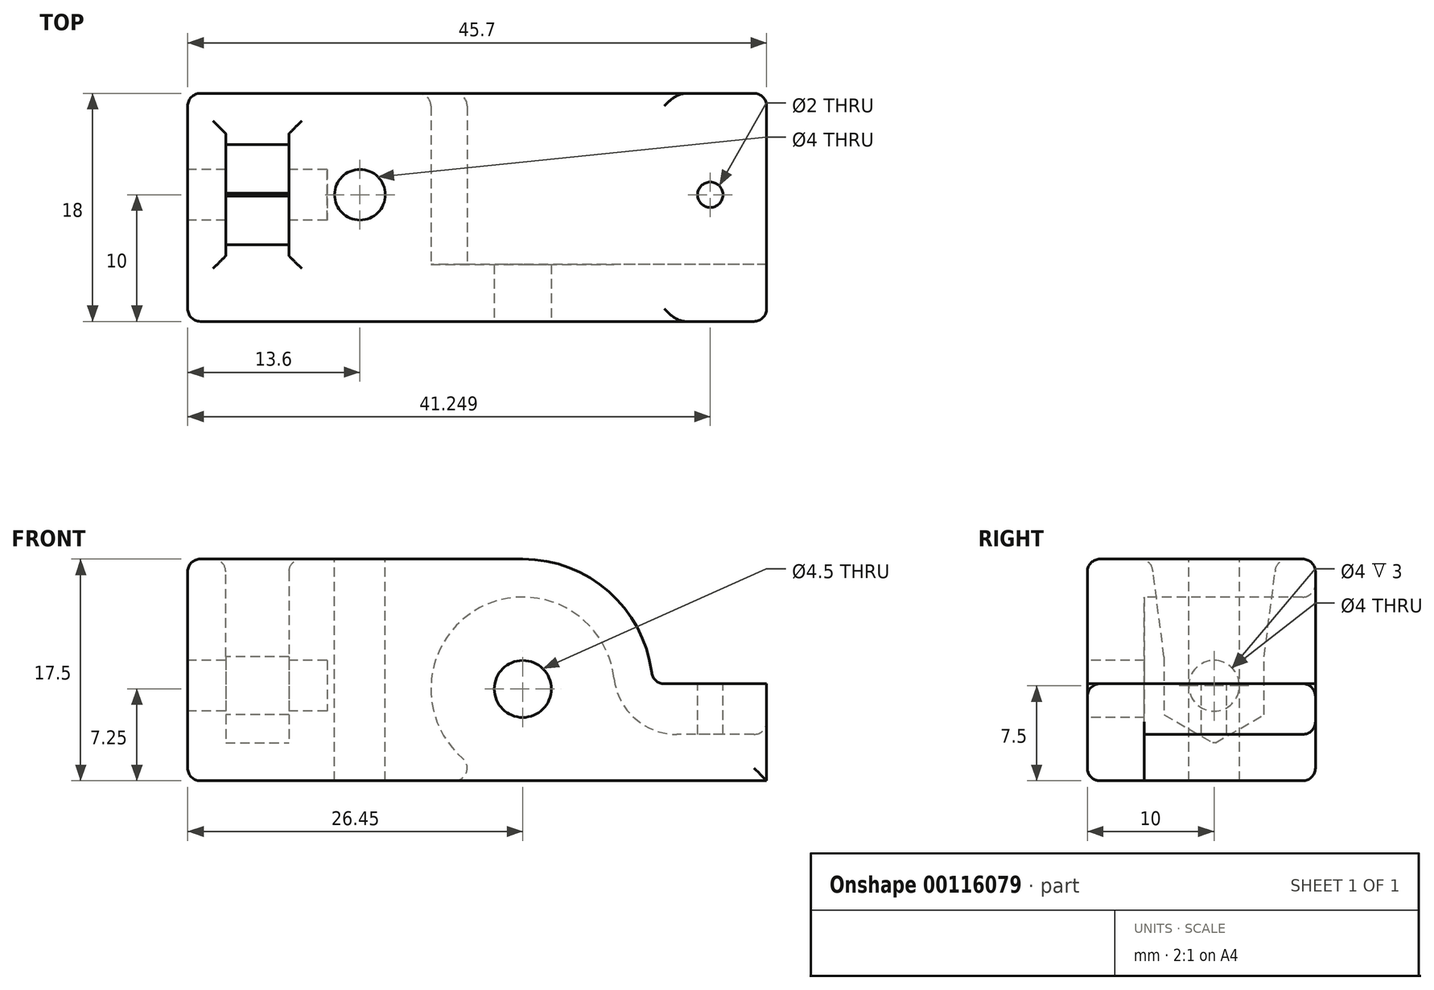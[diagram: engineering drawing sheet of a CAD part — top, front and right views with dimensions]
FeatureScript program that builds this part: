
annotation { "Feature Type Name" : "Feature", "Feature Type Description" : "" }
export const myFeature = defineFeature(function(context is Context, id is Id, definition is map)
    precondition{}
    {
        {
            var Q0;
            Q0=qCreatedBy(makeId("Front.planeOp"),FACE);
            var sketch = newSketch(context, id + "F0", { "sketchPlane" : qUnion([Q0])});
            skLineSegment(sketch, "E0.bottom", {"start": v(-4.4, 17.5) * mm, "end": v(4.4, 17.5) * mm, "construction": true});
            skLineSegment(sketch, "E0.top", {"start": v(-4.4, 21) * mm, "end": v(4.4, 21) * mm, "construction": true});
            skLineSegment(sketch, "E0.left", {"start": v(-4.4, 17.5) * mm, "end": v(-4.4, 21) * mm, "construction": true});
            skLineSegment(sketch, "E0.right", {"start": v(4.4, 17.5) * mm, "end": v(4.4, 21) * mm, "construction": true});
            skLineSegment(sketch, "E1", {"start": v(0, 17.5) * mm, "end": v(0, 0) * mm, "construction": true});
            skLineSegment(sketch, "E2", {"start": v(2.6, 17.5) * mm, "end": v(2.6, 0) * mm, "construction": true});
            skLineSegment(sketch, "E3.MirrorCS", {"start": v(-2.6, 17.5) * mm, "end": v(-2.6, 0) * mm, "construction": true});
            skLineSegment(sketch, "E4.bottom", {"start": v(32.1, 0) * mm, "end": v(-13.6, 0) * mm});
            skLineSegment(sketch, "E4.top", {"start": v(32.1, 17.5) * mm, "end": v(-13.6, 17.5) * mm});
            skLineSegment(sketch, "E4.left", {"start": v(32.1, 0) * mm, "end": v(32.1, 17.5) * mm});
            skLineSegment(sketch, "E4.right", {"start": v(-13.6, 0) * mm, "end": v(-13.6, 17.5) * mm});
            skLineSegment(sketch, "E5", {"start": v(-10.6, 17.5) * mm, "end": v(-10.6, 0) * mm});
            skLineSegment(sketch, "E6", {"start": v(-5.6, 17.5) * mm, "end": v(-5.6, 0) * mm});
            skLineSegment(sketch, "E7", {"start": v(-10.6, 3) * mm, "end": v(-5.6, 3) * mm});
            skLineSegment(sketch, "E8.MirrorCS", {"start": v(-10.6, 12) * mm, "end": v(-5.6, 12) * mm, "construction": true});
            skCircle(sketch, "E9", {"center": v(12.85, 7.25) * mm, "radius": 4.5 * mm});
            skLineSegment(sketch, "E10", {"start": v(32.1, 1.26) * mm, "end": v(36.53, 1.26) * mm, "construction": true});
            skLineSegment(sketch, "E11", {"start": v(32.1, 2.4) * mm, "end": v(36.74, 2.4) * mm, "construction": true});
            skLineSegment(sketch, "E12", {"start": v(32.1, 3.66) * mm, "end": v(36.94, 3.66) * mm, "construction": true});
            skLineSegment(sketch, "E13", {"start": v(32.1, 0) * mm, "end": v(35.76, 0) * mm, "construction": true});
            skCircle(sketch, "E14", {"center": v(12.85, 7.25) * mm, "radius": 7.25 * mm});
            skLineSegment(sketch, "E15", {"start": v(12.85, 0) * mm, "end": v(32.1, 0) * mm});
            skLineSegment(sketch, "E16", {"start": v(32.1, 3.66) * mm, "end": v(19.15, 3.66) * mm});
            skLineSegment(sketch, "E17", {"start": v(-5.6, 10.1) * mm, "end": v(-13.6, 10.1) * mm});
            skLineSegment(sketch, "E18.MirrorCS", {"start": v(-5.6, 4.9) * mm, "end": v(-13.6, 4.9) * mm});
            skPoint(sketch, "E19.orphan", {"position": v(-5.6, 10.1) * mm});
            skPoint(sketch, "E20.orphan", {"position": v(-10.6, 10.1) * mm});
            skLineSegment(sketch, "E21", {"start": v(-13.6, 7.5) * mm, "end": v(-24.03, 7.5) * mm, "construction": true});
            skArc(sketch, "E22.0", {"start": v(23.1, 7.66) * mm, "mid": v(19.95, 14.64) * mm, "end": v(12.85, 17.5) * mm});
            skLineSegment(sketch, "E23", {"start": v(32.1, 7.66) * mm, "end": v(23.1, 7.66) * mm});
            skSolve(sketch);
        }
        {
            var Q0;
            {var subQ1=sQuery(id+"F0.wireOp",EDGE,"E4.bottom");var subQ6=sQuery(id+"F0.wireOp",EDGE,"E4.right");var subQ7=makeQuery(id+"F0.imprint","INTERSECT",VERTEX,{"derivedFrom":[subQ1,subQ6]});Q0=makeQuery(id+"F0.imprint","IMPRINT",FACE,{"disambiguationData":[TD([[makeQuery(id+"F0.imprint","IMPRINT",EDGE,{"disambiguationData":[TD([[subQ7,1.0]])],"derivedFrom":subQ1}),-1.0]])]});}
            var Q1;
            {var subQ5=sQuery(id+"F0.wireOp",EDGE,"E7");Q1=makeQuery(id+"F0.imprint","IMPRINT",FACE,{"disambiguationData":[TD([[makeQuery(id+"F0.imprint","IMPRINT",EDGE,{"derivedFrom":subQ5}),-1.0]])]});}
            var Q2;
            {var subQ3=sQuery(id+"F0.wireOp",EDGE,"E16");Q2=makeQuery(id+"F0.imprint","IMPRINT",FACE,{"disambiguationData":[TD([[makeQuery(id+"F0.imprint","IMPRINT",EDGE,{"derivedFrom":subQ3}),-1.0]])]});}
            var Q3;
            {var subQ0=sQuery(id+"F0.wireOp",EDGE,"E17");var subQ1=sQuery(id+"F0.wireOp",EDGE,"E4.right");var subQ2=makeQuery(id+"F0.imprint","INTERSECT",VERTEX,{"derivedFrom":[subQ1,subQ0]});Q3=makeQuery(id+"F0.imprint","IMPRINT",FACE,{"disambiguationData":[TD([[makeQuery(id+"F0.imprint","IMPRINT",EDGE,{"disambiguationData":[TD([[subQ2,1.0]])],"derivedFrom":subQ1}),-1.0]])]});}
            var Q4;
            {var subQ0=sQuery(id+"F0.wireOp",EDGE,"E4.right");var subQ1=sQuery(id+"F0.wireOp",EDGE,"E4.top");var subQ2=makeQuery(id+"F0.imprint","INTERSECT",VERTEX,{"derivedFrom":[subQ1,subQ0]});Q4=makeQuery(id+"F0.imprint","IMPRINT",FACE,{"disambiguationData":[TD([[makeQuery(id+"F0.imprint","IMPRINT",EDGE,{"disambiguationData":[TD([[subQ2,1.0]])],"derivedFrom":subQ1}),1.0]])]});}
            var Q5;
            {var subQ3=sQuery(id+"F0.wireOp",EDGE,"E22.0");Q5=makeQuery(id+"F0.imprint","IMPRINT",FACE,{"disambiguationData":[TD([[makeQuery(id+"F0.imprint","IMPRINT",EDGE,{"derivedFrom":subQ3}),-1.0]])]});}
            extrude(context, id + "F1", {"entities" : qUnion([Q0, Q1, Q2, Q3, Q4, Q5]), "oppositeDirection" : true, "depth" : 8 * mm, "offsetDistance" : 25 * mm, "hasSecondDirection" : true, "secondDirectionOppositeDirection" : false, "secondDirectionDepth" : 10 * mm});
        }
        {
            var Q0;
            Q0=makeQuery(id+"F1.opExtrude","SWEPT_FACE",FACE,{"disambiguationData":[OSD([sQuery(id+"F0.wireOp",EDGE,"E4.right")])]});
            var sketch = newSketch(context, id + "F2", { "sketchPlane" : qUnion([Q0])});
            skLineSegment(sketch, "E24", {"start": v(0, 0) * mm, "end": v(0, 17.5) * mm, "construction": true});
            skCircle(sketch, "E25", {"center": v(0, 7.5) * mm, "radius": 2.6 * mm, "construction": true});
            skPoint(sketch, "E26.0", {"position": v(0, 12) * mm});
            skPoint(sketch, "E27.0", {"position": v(0, 3) * mm});
            skCircle(sketch, "E28.cCircle", {"center": v(0, 7.5) * mm, "radius": 3.95 * mm, "construction": true});
            skLineSegment(sketch, "E28.0", {"start": v(3.95, 9.78) * mm, "end": v(3.95, 0) * mm});
            skLineSegment(sketch, "E28.1", {"start": v(3.95, 5.22) * mm, "end": v(0, 2.94) * mm});
            skLineSegment(sketch, "E28.2", {"start": v(0, 2.94) * mm, "end": v(-3.95, 5.22) * mm});
            skLineSegment(sketch, "E28.3", {"start": v(-3.95, 0) * mm, "end": v(-3.95, 9.78) * mm});
            skLineSegment(sketch, "E28.4", {"start": v(-3.95, 9.78) * mm, "end": v(0, 12.06) * mm});
            skLineSegment(sketch, "E28.5", {"start": v(0, 12.06) * mm, "end": v(3.95, 9.78) * mm});
            skPoint(sketch, "E28.0.midPoint", {"position": v(3.95, 7.5) * mm});
            skLineSegment(sketch, "E29.bottom", {"start": v(10, 17.5) * mm, "end": v(5.5, 17.5) * mm});
            skLineSegment(sketch, "E29.top", {"start": v(10, 0) * mm, "end": v(5.5, 0) * mm});
            skLineSegment(sketch, "E29.left", {"start": v(10, 17.5) * mm, "end": v(10, 0) * mm});
            skLineSegment(sketch, "E29.right", {"start": v(5.5, 17.5) * mm, "end": v(5.5, 0) * mm});
            skLineSegment(sketch, "E30.0", {"start": v(-8, 0) * mm, "end": v(-8, 17.5) * mm});
            skLineSegment(sketch, "E31", {"start": v(3.95, 9.78) * mm, "end": v(4.95, 17.5) * mm});
            skLineSegment(sketch, "E32", {"start": v(4.95, 17.5) * mm, "end": v(5.5, 17.5) * mm});
            skLineSegment(sketch, "E33.MirrorCS", {"start": v(-3.95, 9.78) * mm, "end": v(-4.95, 17.5) * mm});
            skLineSegment(sketch, "E34.MirrorCS", {"start": v(-4.95, 17.5) * mm, "end": v(-5.5, 17.5) * mm});
            skLineSegment(sketch, "E35.0", {"start": v(-8, 0) * mm, "end": v(10, 0) * mm});
            skLineSegment(sketch, "E36.bottom", {"start": v(-4.5, 2.4) * mm, "end": v(4.5, 2.4) * mm});
            skLineSegment(sketch, "E36.top", {"start": v(-4.5, 0) * mm, "end": v(4.5, 0) * mm});
            skLineSegment(sketch, "E36.left", {"start": v(-4.5, 2.4) * mm, "end": v(-4.5, 0) * mm});
            skLineSegment(sketch, "E36.right", {"start": v(4.5, 2.4) * mm, "end": v(4.5, 0) * mm});
            skPoint(sketch, "E36.middle", {"position": v(0, 1.2) * mm});
            skCircle(sketch, "E37", {"center": v(0, 7.5) * mm, "radius": 2 * mm});
            skLineSegment(sketch, "E38.bottom", {"start": v(12, 11.2) * mm, "end": v(8.5, 11.2) * mm});
            skLineSegment(sketch, "E38.top", {"start": v(12, 3.3) * mm, "end": v(8.5, 3.3) * mm});
            skLineSegment(sketch, "E38.left", {"start": v(12, 11.2) * mm, "end": v(12, 3.3) * mm});
            skLineSegment(sketch, "E38.right", {"start": v(8.5, 11.2) * mm, "end": v(8.5, 3.3) * mm});
            skPoint(sketch, "E39.0", {"position": v(0, 7.25) * mm});
            skLineSegment(sketch, "E40", {"start": v(0, 7.25) * mm, "end": v(15.95, 7.25) * mm, "construction": true});
            skSolve(sketch);
        }
        {
            var Q0;
            Q0=makeQuery(id+"F2.imprint","IMPRINT",FACE,{"disambiguationData":[TD([[makeQuery(id+"F2.imprint","IMPRINT",EDGE,{"derivedFrom":sQuery(id+"F2.wireOp",EDGE,"E37")}),1.0]])]});
            var Q1;
            Q1=sQuery(id+"F6.wireOp",EDGE,"IWxHj1E6-c78I-Bpa6-nnZ4-fiathDjzlDGy");
            var Q2;
            Q2=sQuery(id+"F6.wireOp",EDGE,"G7mef5TC-vuGq-qOCV-Zkp3-S8K1r66uwu5S");
            var Q3;
            Q3=makeQuery(id+"F1.opExtrude","SWEPT_FACE",FACE,{"disambiguationData":[OSD([sQuery(id+"F0.wireOp",EDGE,"E6")])]});
            extrude(context, id + "F3", {"entities" : qUnion([Q0]), "operationType" : NewBodyOperationType.REMOVE, "surfaceEntities" : qUnion([Q1, Q2]), "endBound" : BoundingType.UP_TO_SURFACE, "oppositeDirection" : true, "depth" : 25 * mm, "endBoundEntityFace" : qUnion([Q3]), "hasOffset" : true, "offsetDistance" : 3 * mm, "offsetOppositeDirection" : true});
        }
        {
            var Q0;
            {var subQ0=sQuery(id+"F2.wireOp",EDGE,"E30.0");Q0=makeQuery(id+"F2.imprint","IMPRINT",FACE,{"disambiguationData":[TD([[makeQuery(id+"F2.imprint","IMPRINT",EDGE,{"derivedFrom":subQ0}),-1.0]])]});}
            var Q1;
            {var subQ5=sQuery(id+"F2.wireOp",EDGE,"E29.right");Q1=makeQuery(id+"F2.imprint","IMPRINT",FACE,{"disambiguationData":[TD([[makeQuery(id+"F2.imprint","IMPRINT",EDGE,{"derivedFrom":subQ5}),-1.0]])]});}
            var Q2;
            {var subQ4=sQuery(id+"F2.wireOp",EDGE,"E28.1");Q2=makeQuery(id+"F2.imprint","IMPRINT",FACE,{"disambiguationData":[TD([[makeQuery(id+"F2.imprint","IMPRINT",EDGE,{"derivedFrom":subQ4}),1.0]])]});}
            var Q3;
            Q3=makeQuery(id+"F1.opExtrude","SWEPT_FACE",FACE,{"disambiguationData":[OSD([sQuery(id+"F0.wireOp",EDGE,"E6")])]});
            extrude(context, id + "F4", {"entities" : qUnion([Q0, Q1, Q2]), "operationType" : NewBodyOperationType.ADD, "endBound" : BoundingType.UP_TO_SURFACE, "oppositeDirection" : true, "depth" : 25 * mm, "endBoundEntityFace" : qUnion([Q3]), "offsetDistance" : 25 * mm});
        }
        {
            var Q0;
            {var subQ2=sQuery(id+"F2.wireOp",EDGE,"E29.bottom");Q0=makeQuery(id+"F2.imprint","IMPRINT",FACE,{"disambiguationData":[TD([[makeQuery(id+"F2.imprint","IMPRINT",EDGE,{"derivedFrom":subQ2}),-1.0]])]});}
            var Q1;
            {var subQ5=sQuery(id+"F2.wireOp",EDGE,"E38.right");Q1=makeQuery(id+"F2.imprint","IMPRINT",FACE,{"disambiguationData":[TD([[makeQuery(id+"F2.imprint","IMPRINT",EDGE,{"derivedFrom":subQ5}),1.0]])]});}
            var Q2;
            {var subQ0=sQuery(id+"F0.wireOp",EDGE,"E4.left");Q2=makeQuery(id+"F1.opExtrude","SWEPT_FACE",FACE,{"disambiguationData":[OSD([subQ0]),TDD([makeQuery(id+"F0.imprint","IMPRINT",EDGE,{"disambiguationData":[TD([[makeQuery(id+"F0.imprint","INTERSECT",VERTEX,{"derivedFrom":[subQ0,sQuery(id+"F0.wireOp",EDGE,"E16")]}),-1.0]])],"derivedFrom":subQ0})])]});}
            extrude(context, id + "F5", {"entities" : qUnion([Q0, Q1]), "operationType" : NewBodyOperationType.ADD, "endBound" : BoundingType.UP_TO_SURFACE, "oppositeDirection" : true, "depth" : 7 * mm, "endBoundEntityFace" : qUnion([Q2]), "offsetDistance" : 2 * mm});
        }
        {
            var Q0;
            {var subQ0=sQuery(id+"F0.wireOp",EDGE,"E4.left");Q0=makeQuery(id+"F5.boolean.opBoolean","MERGE",FACE,{"derivedFrom":[makeQuery(id+"F1.opExtrude","SWEPT_FACE",FACE,{"disambiguationData":[OSD([subQ0]),TDD([makeQuery(id+"F0.imprint","IMPRINT",EDGE,{"disambiguationData":[TD([[makeQuery(id+"F0.imprint","INTERSECT",VERTEX,{"derivedFrom":[sQuery(id+"F0.wireOp",EDGE,"E4.bottom"),subQ0]}),-1.0]])],"derivedFrom":subQ0})])]}),makeQuery(id+"F1.opExtrude","SWEPT_FACE",FACE,{"disambiguationData":[OSD([subQ0]),TDD([makeQuery(id+"F0.imprint","IMPRINT",EDGE,{"disambiguationData":[TD([[makeQuery(id+"F0.imprint","INTERSECT",VERTEX,{"derivedFrom":[sQuery(id+"F0.wireOp",EDGE,"E4.top"),subQ0]}),1.0]])],"derivedFrom":subQ0})])]}),makeQuery(id+"F5.opExtrude","CAP_FACE",FACE,{"disambiguationData":[OSD([sQuery(id+"F2.wireOp",EDGE,"E29.bottom"),sQuery(id+"F2.wireOp",EDGE,"E29.left"),sQuery(id+"F2.wireOp",EDGE,"E29.right"),sQuery(id+"F2.wireOp",EDGE,"E35.0")])],"isStart":false})]});}
            var sketch = newSketch(context, id + "F6", { "sketchPlane" : qUnion([Q0])});
            skLineSegment(sketch, "E41", {"start": v(0, 0) * mm, "end": v(0, 10.25) * mm, "construction": true});
            skLineSegment(sketch, "E42.bottom", {"start": v(4.5, 17.5) * mm, "end": v(-4.5, 17.5) * mm, "construction": true});
            skLineSegment(sketch, "E42.top", {"start": v(4.5, 18.76) * mm, "end": v(-4.5, 18.76) * mm, "construction": true});
            skLineSegment(sketch, "E42.left", {"start": v(4.5, 17.5) * mm, "end": v(4.5, 18.76) * mm, "construction": true});
            skLineSegment(sketch, "E42.right", {"start": v(-4.5, 17.5) * mm, "end": v(-4.5, 18.76) * mm, "construction": true});
            skPoint(sketch, "E42.middle", {"position": v(0, 18.13) * mm});
            skLineSegment(sketch, "E43", {"start": v(-4.5, 18.76) * mm, "end": v(-4.5, 19.9) * mm, "construction": true});
            skLineSegment(sketch, "E44", {"start": v(-4.5, 19.9) * mm, "end": v(4.5, 19.9) * mm, "construction": true});
            skLineSegment(sketch, "E45", {"start": v(4.5, 19.9) * mm, "end": v(4.5, 18.76) * mm, "construction": true});
            skLineSegment(sketch, "E46", {"start": v(-4.5, 19.9) * mm, "end": v(-4.5, 21.16) * mm, "construction": true});
            skLineSegment(sketch, "E47", {"start": v(-4.5, 21.16) * mm, "end": v(4.5, 21.16) * mm, "construction": true});
            skLineSegment(sketch, "E48", {"start": v(4.5, 21.16) * mm, "end": v(4.5, 19.9) * mm, "construction": true});
            skCircle(sketch, "E49.0", {"center": v(0, 7.5) * mm, "radius": 2 * mm, "construction": true});
            skSolve(sketch);
        }
        {
            var Q0;
            {var subQ0=sQuery(id+"F0.wireOp",EDGE,"E4.right");var subQ1=sQuery(id+"F0.wireOp",EDGE,"E4.top");Q0=makeQuery(id+"F5.boolean.opBoolean","MERGE",FACE,{"derivedFrom":[makeQuery(id+"F4.boolean.opBoolean","MERGE",FACE,{"derivedFrom":[makeQuery(id+"F1.opExtrude","SWEPT_FACE",FACE,{"disambiguationData":[OSD([subQ1]),TDD([makeQuery(id+"F0.imprint","IMPRINT",EDGE,{"disambiguationData":[TD([[makeQuery(id+"F0.imprint","INTERSECT",VERTEX,{"derivedFrom":[subQ1,sQuery(id+"F0.wireOp",EDGE,"E4.left")]}),-1.0]])],"derivedFrom":subQ1})])]}),makeQuery(id+"F1.opExtrude","SWEPT_FACE",FACE,{"disambiguationData":[OSD([subQ1]),TDD([makeQuery(id+"F0.imprint","IMPRINT",EDGE,{"disambiguationData":[TD([[makeQuery(id+"F0.imprint","INTERSECT",VERTEX,{"derivedFrom":[subQ1,subQ0]}),1.0]])],"derivedFrom":subQ1})])]}),makeQuery(id+"F4.opExtrude","SWEPT_FACE",FACE,{"disambiguationData":[OSD([sQuery(id+"F2.wireOp",EDGE,"E32")])]}),makeQuery(id+"F4.opExtrude","SWEPT_FACE",FACE,{"disambiguationData":[OSD([subQ1,subQ0,sQuery(id+"F2.wireOp",EDGE,"E34.MirrorCS")])]})]}),makeQuery(id+"F5.opExtrude","SWEPT_FACE",FACE,{"disambiguationData":[OSD([sQuery(id+"F2.wireOp",EDGE,"E29.bottom")])]})]});}
            var sketch = newSketch(context, id + "F7", { "sketchPlane" : qUnion([Q0])});
            skCircle(sketch, "E50", {"center": v(0, 0) * mm, "radius": 2 * mm});
            skLineSegment(sketch, "E51.0", {"start": v(19.15, 8) * mm, "end": v(19.15, -5.5) * mm, "construction": true});
            skLineSegment(sketch, "E52", {"start": v(19.15, 0) * mm, "end": v(36.15, 0) * mm, "construction": true});
            skCircle(sketch, "E53", {"center": v(27.65, 0) * mm, "radius": 1 * mm});
            skCircle(sketch, "E54", {"center": v(27.65, 0) * mm, "radius": 3 * mm, "construction": true});
            skSolve(sketch);
        }
        {
            var Q0;
            Q0=makeQuery(id+"F7.imprint","IMPRINT",FACE,{"disambiguationData":[TD([[makeQuery(id+"F7.imprint","IMPRINT",EDGE,{"derivedFrom":sQuery(id+"F7.wireOp",EDGE,"E50")}),1.0]])]});
            var Q1;
            Q1=makeQuery(id+"F7.imprint","IMPRINT",FACE,{"disambiguationData":[TD([[makeQuery(id+"F7.imprint","IMPRINT",EDGE,{"derivedFrom":sQuery(id+"F7.wireOp",EDGE,"E53")}),1.0]])]});
            extrude(context, id + "F8", {"entities" : qUnion([Q0, Q1]), "operationType" : NewBodyOperationType.REMOVE, "oppositeDirection" : true, "depth" : 25 * mm, "offsetDistance" : 25 * mm});
        }
        {
            var Q0;
            {var subQ3=sQuery(id+"F0.wireOp",EDGE,"E22.0");Q0=makeQuery(id+"F0.imprint","IMPRINT",FACE,{"disambiguationData":[TD([[makeQuery(id+"F0.imprint","IMPRINT",EDGE,{"derivedFrom":subQ3}),-1.0]])]});}
            extrude(context, id + "F9", {"entities" : qUnion([Q0]), "operationType" : NewBodyOperationType.REMOVE, "endBound" : BoundingType.SYMMETRIC, "depth" : 25 * mm, "offsetDistance" : 25 * mm});
        }
        {
            var Q0;
            Q0=makeQuery(id+"F5.boolean.opBoolean","MERGE",FACE,{"derivedFrom":[makeQuery(id+"F1.opExtrude","CAP_FACE",FACE,{"disambiguationData":[OSD([sQuery(id+"F0.wireOp",EDGE,"E4.bottom"),sQuery(id+"F0.wireOp",EDGE,"E4.top"),sQuery(id+"F0.wireOp",EDGE,"E4.left"),sQuery(id+"F0.wireOp",EDGE,"E4.right"),sQuery(id+"F0.wireOp",EDGE,"E5"),sQuery(id+"F0.wireOp",EDGE,"E6"),sQuery(id+"F0.wireOp",EDGE,"E7"),sQuery(id+"F0.wireOp",EDGE,"E14"),sQuery(id+"F0.wireOp",EDGE,"E15"),sQuery(id+"F0.wireOp",EDGE,"E16")])],"isStart":true}),makeQuery(id+"F5.opExtrude","SWEPT_FACE",FACE,{"disambiguationData":[OSD([sQuery(id+"F2.wireOp",EDGE,"E29.left")])]})]});
            var sketch = newSketch(context, id + "F10", { "sketchPlane" : qUnion([Q0])});
            skCircle(sketch, "E55.0", {"center": v(12.85, 7.25) * mm, "radius": 4.5 * mm, "construction": true});
            skCircle(sketch, "E56", {"center": v(12.85, 7.25) * mm, "radius": 2.25 * mm});
            skCircle(sketch, "E57.cCircle", {"center": v(12.85, 7.25) * mm, "radius": 4.25 * mm, "construction": true});
            skLineSegment(sketch, "E57.0", {"start": v(17.1, 9.7) * mm, "end": v(17.1, 4.8) * mm});
            skLineSegment(sketch, "E57.1", {"start": v(17.1, 4.8) * mm, "end": v(12.85, 2.34) * mm});
            skLineSegment(sketch, "E57.2", {"start": v(12.85, 2.34) * mm, "end": v(8.6, 4.8) * mm});
            skLineSegment(sketch, "E57.3", {"start": v(8.6, 4.8) * mm, "end": v(8.6, 9.7) * mm});
            skLineSegment(sketch, "E57.4", {"start": v(8.6, 9.7) * mm, "end": v(12.85, 12.16) * mm});
            skLineSegment(sketch, "E57.5", {"start": v(12.85, 12.16) * mm, "end": v(17.1, 9.7) * mm});
            skPoint(sketch, "E57.0.midPoint", {"position": v(17.1, 7.25) * mm});
            skSolve(sketch);
        }
        {
            var Q0;
            Q0=makeQuery(id+"F10.imprint","IMPRINT",FACE,{"disambiguationData":[TD([[makeQuery(id+"F10.imprint","IMPRINT",EDGE,{"derivedFrom":sQuery(id+"F10.wireOp",EDGE,"E56")}),1.0]])]});
            extrude(context, id + "F11", {"entities" : qUnion([Q0]), "operationType" : NewBodyOperationType.REMOVE, "oppositeDirection" : true, "depth" : 25 * mm, "offsetDistance" : 25 * mm});
        }
        {
            var Q0;
            Q0=makeQuery(id+"F1.opExtrude","SWEPT_EDGE",EDGE,{"disambiguationData":[OSD([sQuery(id+"F0.wireOp",EDGE,"E14"),sQuery(id+"F0.wireOp",EDGE,"E16")])]});
            fillet(context, id + "F12", {"entities" : qUnion([Q0]), "radius" : 5 * mm, "tangentPropagation" : true, "allowEdgeOverflow" : false});
        }
        {
            var Q0;
            Q0=makeQuery(id+"F1.opExtrude","CAP_EDGE",EDGE,{"disambiguationData":[OSD([sQuery(id+"F0.wireOp",EDGE,"E14")])],"isStart":false});
            var Q1;
            {var subQ0=sQuery(id+"F0.wireOp",EDGE,"E16");var subQ1=sQuery(id+"F0.wireOp",EDGE,"E14");Q1=makeQuery(id+"F12.opFillet","BLEND_EDGE",EDGE,{"blendedFrom":[makeQuery(id+"F1.opExtrude","SWEPT_EDGE",EDGE,{"disambiguationData":[OSD([subQ1,subQ0])]}),makeQuery(id+"F4.boolean.opBoolean","MERGE",FACE,{"derivedFrom":[makeQuery(id+"F1.opExtrude","CAP_FACE",FACE,{"disambiguationData":[OSD([sQuery(id+"F0.wireOp",EDGE,"E4.bottom"),sQuery(id+"F0.wireOp",EDGE,"E4.top"),sQuery(id+"F0.wireOp",EDGE,"E4.left"),sQuery(id+"F0.wireOp",EDGE,"E4.right"),sQuery(id+"F0.wireOp",EDGE,"E5"),sQuery(id+"F0.wireOp",EDGE,"E6"),sQuery(id+"F0.wireOp",EDGE,"E7"),subQ1,subQ0,sQuery(id+"F0.wireOp",EDGE,"E22.0"),sQuery(id+"F0.wireOp",EDGE,"E23")])],"isStart":false}),makeQuery(id+"F4.opExtrude","SWEPT_FACE",FACE,{"disambiguationData":[OSD([sQuery(id+"F2.wireOp",EDGE,"E30.0")])]})]})],"blendedInto":[makeQuery(id+"F4.boolean.opBoolean","MERGE",FACE,{"derivedFrom":[makeQuery(id+"F1.opExtrude","CAP_FACE",FACE,{"disambiguationData":[OSD([sQuery(id+"F0.wireOp",EDGE,"E4.bottom"),sQuery(id+"F0.wireOp",EDGE,"E4.top"),sQuery(id+"F0.wireOp",EDGE,"E4.left"),sQuery(id+"F0.wireOp",EDGE,"E4.right"),sQuery(id+"F0.wireOp",EDGE,"E5"),sQuery(id+"F0.wireOp",EDGE,"E6"),sQuery(id+"F0.wireOp",EDGE,"E7"),subQ1,subQ0,sQuery(id+"F0.wireOp",EDGE,"E22.0"),sQuery(id+"F0.wireOp",EDGE,"E23")])],"isStart":false}),makeQuery(id+"F4.opExtrude","SWEPT_FACE",FACE,{"disambiguationData":[OSD([sQuery(id+"F2.wireOp",EDGE,"E30.0")])]})]})]});}
            var Q2;
            {var subQ0=sQuery(id+"F0.wireOp",EDGE,"E4.right");var subQ1=sQuery(id+"F0.wireOp",EDGE,"E4.top");Q2=makeQuery(id+"F4.boolean.opBoolean","MERGE",EDGE,{"derivedFrom":[makeQuery(id+"F1.opExtrude","CAP_EDGE",EDGE,{"disambiguationData":[OSD([subQ1]),TDD([makeQuery(id+"F0.imprint","IMPRINT",EDGE,{"disambiguationData":[TD([[makeQuery(id+"F0.imprint","INTERSECT",VERTEX,{"derivedFrom":[subQ1,sQuery(id+"F0.wireOp",EDGE,"E6")]}),1.0]])],"derivedFrom":subQ1})])],"isStart":false}),makeQuery(id+"F1.opExtrude","CAP_EDGE",EDGE,{"disambiguationData":[OSD([subQ1]),TDD([makeQuery(id+"F0.imprint","IMPRINT",EDGE,{"disambiguationData":[TD([[makeQuery(id+"F0.imprint","INTERSECT",VERTEX,{"derivedFrom":[subQ1,subQ0]}),1.0]])],"derivedFrom":subQ1})])],"isStart":false}),makeQuery(id+"F4.opExtrude","SWEPT_EDGE",EDGE,{"disambiguationData":[OSD([subQ1,subQ0,sQuery(id+"F2.wireOp",EDGE,"E30.0")])]})]});}
            var Q3;
            {var subQ0=sQuery(id+"F0.wireOp",EDGE,"E4.top");Q3=makeQuery(id+"F5.boolean.opBoolean","MERGE",EDGE,{"derivedFrom":[makeQuery(id+"F1.opExtrude","CAP_EDGE",EDGE,{"disambiguationData":[OSD([subQ0]),TDD([makeQuery(id+"F0.imprint","IMPRINT",EDGE,{"disambiguationData":[TD([[makeQuery(id+"F0.imprint","INTERSECT",VERTEX,{"derivedFrom":[subQ0,sQuery(id+"F0.wireOp",EDGE,"E6")]}),1.0]])],"derivedFrom":subQ0})])],"isStart":true}),makeQuery(id+"F1.opExtrude","CAP_EDGE",EDGE,{"disambiguationData":[OSD([subQ0]),TDD([makeQuery(id+"F0.imprint","IMPRINT",EDGE,{"disambiguationData":[TD([[makeQuery(id+"F0.imprint","INTERSECT",VERTEX,{"derivedFrom":[subQ0,sQuery(id+"F0.wireOp",EDGE,"E4.right")]}),1.0]])],"derivedFrom":subQ0})])],"isStart":true}),makeQuery(id+"F5.opExtrude","SWEPT_EDGE",EDGE,{"disambiguationData":[OSD([sQuery(id+"F2.wireOp",EDGE,"E29.bottom"),sQuery(id+"F2.wireOp",EDGE,"E29.left")])]})]});}
            var Q4;
            Q4=makeQuery(id+"F1.opExtrude","CAP_EDGE",EDGE,{"disambiguationData":[OSD([sQuery(id+"F0.wireOp",EDGE,"E4.bottom")])],"isStart":false});
            var Q5;
            Q5=makeQuery(id+"F5.boolean.opBoolean","MERGE",EDGE,{"derivedFrom":[makeQuery(id+"F1.opExtrude","CAP_EDGE",EDGE,{"disambiguationData":[OSD([sQuery(id+"F0.wireOp",EDGE,"E4.bottom")])],"isStart":true}),makeQuery(id+"F5.opExtrude","SWEPT_EDGE",EDGE,{"disambiguationData":[OSD([sQuery(id+"F2.wireOp",EDGE,"E29.left"),sQuery(id+"F2.wireOp",EDGE,"E35.0")])]})]});
            var Q6;
            Q6=makeQuery(id+"F1.opExtrude","SWEPT_EDGE",EDGE,{"disambiguationData":[OSD([sQuery(id+"F0.wireOp",EDGE,"E4.left"),sQuery(id+"F0.wireOp",EDGE,"E16")])]});
            var Q7;
            Q7=makeQuery(id+"F1.opExtrude","SWEPT_EDGE",EDGE,{"disambiguationData":[OSD([sQuery(id+"F0.wireOp",EDGE,"E4.bottom"),sQuery(id+"F0.wireOp",EDGE,"E4.right")])]});
            var Q8;
            {var subQ0=sQuery(id+"F0.wireOp",EDGE,"E23");var subQ1=sQuery(id+"F0.wireOp",EDGE,"E4.left");Q8=makeQuery(id+"F9.boolean.opBoolean","MERGE",EDGE,{"derivedFrom":[makeQuery(id+"F1.opExtrude","SWEPT_EDGE",EDGE,{"disambiguationData":[OSD([subQ1,subQ0])]}),makeQuery(id+"F9.opExtrude","SWEPT_EDGE",EDGE,{"disambiguationData":[OSD([subQ1,subQ0])]})]});}
            var Q9;
            {var subQ0=sQuery(id+"F0.wireOp",EDGE,"E5");var subQ2=sQuery(id+"F0.wireOp",EDGE,"E4.top");Q9=makeQuery(id+"F4.boolean.opBoolean","SPLIT",EDGE,{"disambiguationData":[TD([makeQuery(id+"F4.opExtrude","SWEPT_FACE",FACE,{"disambiguationData":[OSD([sQuery(id+"F2.wireOp",EDGE,"E31")])]})])],"derivedFrom":makeQuery(id+"F1.opExtrude","SWEPT_EDGE",EDGE,{"disambiguationData":[OSD([subQ2,subQ0])]})});}
            var Q10;
            {var subQ1=sQuery(id+"F0.wireOp",EDGE,"E4.top");var subQ2=sQuery(id+"F0.wireOp",EDGE,"E6");Q10=makeQuery(id+"F4.boolean.opBoolean","SPLIT",EDGE,{"disambiguationData":[TD([makeQuery(id+"F4.opExtrude","SWEPT_FACE",FACE,{"disambiguationData":[OSD([sQuery(id+"F2.wireOp",EDGE,"E31")])]})])],"derivedFrom":makeQuery(id+"F1.opExtrude","SWEPT_EDGE",EDGE,{"disambiguationData":[OSD([subQ1,subQ2])]})});}
            var Q11;
            Q11=makeQuery(id+"F1.opExtrude","SWEPT_EDGE",EDGE,{"disambiguationData":[OSD([sQuery(id+"F0.wireOp",EDGE,"E4.top"),sQuery(id+"F0.wireOp",EDGE,"E4.right")])]});
            var Q12;
            {var subQ0=sQuery(id+"F2.wireOp",EDGE,"E29.left");var subQ2=makeQuery(id+"F2.imprint","INTERSECT",VERTEX,{"derivedFrom":[subQ0,sQuery(id+"F2.wireOp",EDGE,"E38.top")]});var subQ3=sQuery(id+"F0.wireOp",EDGE,"E4.left");Q12=makeQuery(id+"F5.boolean.opBoolean","MERGE",EDGE,{"derivedFrom":[makeQuery(id+"F1.opExtrude","CAP_EDGE",EDGE,{"disambiguationData":[OSD([subQ3])],"isStart":true}),makeQuery(id+"F5.opExtrude","TWEAK_EDGE",EDGE,{"derivedFrom":[makeQuery(id+"F1.opExtrude","SWEPT_FACE",FACE,{"disambiguationData":[OSD([subQ3])]}),makeQuery(id+"F2.imprint","IMPRINT",EDGE,{"disambiguationData":[TD([[makeQuery(id+"F2.imprint","INTERSECT",VERTEX,{"derivedFrom":[subQ0,sQuery(id+"F2.wireOp",EDGE,"E35.0")]}),-1.0]])],"derivedFrom":subQ0}),makeQuery(id+"F2.imprint","IMPRINT",EDGE,{"disambiguationData":[TD([[subQ2,-1.0]])],"derivedFrom":subQ0}),makeQuery(id+"F2.imprint","IMPRINT",EDGE,{"disambiguationData":[TD([[makeQuery(id+"F2.imprint","INTERSECT",VERTEX,{"derivedFrom":[sQuery(id+"F2.wireOp",EDGE,"E29.bottom"),subQ0]}),1.0]])],"derivedFrom":subQ0})]})]});}
            var Q13;
            Q13=makeQuery(id+"F1.opExtrude","CAP_EDGE",EDGE,{"disambiguationData":[OSD([sQuery(id+"F0.wireOp",EDGE,"E4.right")])],"isStart":true});
            var Q14;
            Q14=makeQuery(id+"F1.opExtrude","CAP_EDGE",EDGE,{"disambiguationData":[OSD([sQuery(id+"F0.wireOp",EDGE,"E4.right")])],"isStart":false});
            var Q15;
            Q15=makeQuery(id+"F4.opExtrude","SWEPT_EDGE",EDGE,{"disambiguationData":[OSD([sQuery(id+"F0.wireOp",EDGE,"E4.top"),sQuery(id+"F0.wireOp",EDGE,"E4.right"),sQuery(id+"F2.wireOp",EDGE,"E31"),sQuery(id+"F2.wireOp",EDGE,"E32")])]});
            var Q16;
            Q16=makeQuery(id+"F4.opExtrude","SWEPT_EDGE",EDGE,{"disambiguationData":[OSD([sQuery(id+"F0.wireOp",EDGE,"E4.top"),sQuery(id+"F0.wireOp",EDGE,"E4.right"),sQuery(id+"F2.wireOp",EDGE,"E33.MirrorCS"),sQuery(id+"F2.wireOp",EDGE,"E34.MirrorCS")])]});
            var Q17;
            {var subQ0=sQuery(id+"F0.wireOp",EDGE,"E23");var subQ1=sQuery(id+"F0.wireOp",EDGE,"E22.0");Q17=makeQuery(id+"F9.boolean.opBoolean","MERGE",EDGE,{"derivedFrom":[makeQuery(id+"F1.opExtrude","SWEPT_EDGE",EDGE,{"disambiguationData":[OSD([subQ1,subQ0])]}),makeQuery(id+"F9.opExtrude","SWEPT_EDGE",EDGE,{"disambiguationData":[OSD([subQ1,subQ0])]})]});}
            var Q18;
            Q18=makeQuery(id+"F1.opExtrude","SWEPT_EDGE",EDGE,{"disambiguationData":[OSD([sQuery(id+"F0.wireOp",EDGE,"E4.bottom"),sQuery(id+"F0.wireOp",EDGE,"E14"),sQuery(id+"F0.wireOp",EDGE,"E15")])]});
            var Q19;
            {var subQ0=sQuery(id+"F0.wireOp",EDGE,"E22.0");var subQ1=sQuery(id+"F0.wireOp",EDGE,"E4.top");Q19=makeQuery(id+"F9.boolean.opBoolean","MERGE",EDGE,{"derivedFrom":[makeQuery(id+"F1.opExtrude","SWEPT_EDGE",EDGE,{"disambiguationData":[OSD([subQ1,subQ0])]}),makeQuery(id+"F9.opExtrude","SWEPT_EDGE",EDGE,{"disambiguationData":[OSD([subQ1,subQ0])]})]});}
            var Q20;
            Q20=makeQuery(id+"F9.boolean.opBoolean","COPY",EDGE,{"derivedFrom":makeQuery(id+"F9.opExtrude","SWEPT_EDGE",EDGE,{"disambiguationData":[OSD([sQuery(id+"F0.wireOp",EDGE,"E22.0"),sQuery(id+"F0.wireOp",EDGE,"E23")])]})});
            var Q21;
            Q21=makeQuery(id+"F9.boolean.opBoolean","COPY",EDGE,{"derivedFrom":makeQuery(id+"F9.opExtrude","SWEPT_EDGE",EDGE,{"disambiguationData":[OSD([sQuery(id+"F0.wireOp",EDGE,"E4.top"),sQuery(id+"F0.wireOp",EDGE,"E22.0")])]})});
            var Q22;
            Q22=makeQuery(id+"F9.boolean.opBoolean","INTERSECT",EDGE,{"derivedFrom":[makeQuery(id+"F5.boolean.opBoolean","MERGE",FACE,{"derivedFrom":[makeQuery(id+"F1.opExtrude","CAP_FACE",FACE,{"disambiguationData":[OSD([sQuery(id+"F0.wireOp",EDGE,"E4.bottom"),sQuery(id+"F0.wireOp",EDGE,"E4.top"),sQuery(id+"F0.wireOp",EDGE,"E4.left"),sQuery(id+"F0.wireOp",EDGE,"E4.right"),sQuery(id+"F0.wireOp",EDGE,"E5"),sQuery(id+"F0.wireOp",EDGE,"E6"),sQuery(id+"F0.wireOp",EDGE,"E7"),sQuery(id+"F0.wireOp",EDGE,"E14"),sQuery(id+"F0.wireOp",EDGE,"E15"),sQuery(id+"F0.wireOp",EDGE,"E16")])],"isStart":true}),makeQuery(id+"F5.opExtrude","SWEPT_FACE",FACE,{"disambiguationData":[OSD([sQuery(id+"F2.wireOp",EDGE,"E29.left")])]})]}),makeQuery(id+"F9.opExtrude","SWEPT_FACE",FACE,{"disambiguationData":[OSD([sQuery(id+"F0.wireOp",EDGE,"E22.0")])]})]});
            var Q23;
            Q23=makeQuery(id+"F9.boolean.opBoolean","INTERSECT",EDGE,{"derivedFrom":[makeQuery(id+"F4.boolean.opBoolean","MERGE",FACE,{"derivedFrom":[makeQuery(id+"F1.opExtrude","CAP_FACE",FACE,{"disambiguationData":[OSD([sQuery(id+"F0.wireOp",EDGE,"E4.bottom"),sQuery(id+"F0.wireOp",EDGE,"E4.top"),sQuery(id+"F0.wireOp",EDGE,"E4.left"),sQuery(id+"F0.wireOp",EDGE,"E4.right"),sQuery(id+"F0.wireOp",EDGE,"E5"),sQuery(id+"F0.wireOp",EDGE,"E6"),sQuery(id+"F0.wireOp",EDGE,"E7"),sQuery(id+"F0.wireOp",EDGE,"E14"),sQuery(id+"F0.wireOp",EDGE,"E15"),sQuery(id+"F0.wireOp",EDGE,"E16")])],"isStart":false}),makeQuery(id+"F4.opExtrude","SWEPT_FACE",FACE,{"disambiguationData":[OSD([sQuery(id+"F2.wireOp",EDGE,"E30.0")])]})]}),makeQuery(id+"F9.opExtrude","SWEPT_FACE",FACE,{"disambiguationData":[OSD([sQuery(id+"F0.wireOp",EDGE,"E22.0")])]})]});
            var Q24;
            Q24=makeQuery(id+"F9.boolean.opBoolean","COPY",EDGE,{"derivedFrom":makeQuery(id+"F9.opExtrude","SWEPT_EDGE",EDGE,{"disambiguationData":[OSD([sQuery(id+"F0.wireOp",EDGE,"E4.left"),sQuery(id+"F0.wireOp",EDGE,"E23")])]})});
            var Q25;
            {var subQ0=sQuery(id+"F0.wireOp",EDGE,"E4.left");Q25=makeQuery(id+"F1.opExtrude","CAP_EDGE",EDGE,{"disambiguationData":[OSD([subQ0]),TDD([makeQuery(id+"F0.imprint","IMPRINT",EDGE,{"disambiguationData":[TD([[makeQuery(id+"F0.imprint","INTERSECT",VERTEX,{"derivedFrom":[subQ0,sQuery(id+"F0.wireOp",EDGE,"E16")]}),-1.0]])],"derivedFrom":subQ0}),makeQuery(id+"F0.imprint","IMPRINT",EDGE,{"disambiguationData":[TD([[makeQuery(id+"F0.imprint","INTERSECT",VERTEX,{"derivedFrom":[sQuery(id+"F0.wireOp",EDGE,"E4.top"),subQ0]}),1.0]])],"derivedFrom":subQ0})])],"isStart":false});}
            var Q26;
            Q26=makeQuery(id+"F1.opExtrude","CAP_EDGE",EDGE,{"disambiguationData":[OSD([sQuery(id+"F0.wireOp",EDGE,"E4.bottom")])],"isStart":true});
            fillet(context, id + "F13", {"entities" : qUnion([Q0, Q1, Q2, Q3, Q4, Q5, Q6, Q7, Q8, Q9, Q10, Q11, Q12, Q13, Q14, Q15, Q16, Q17, Q18, Q19, Q20, Q21, Q22, Q23, Q24, Q25, Q26]), "radius" : 1 * mm, "tangentPropagation" : true, "allowEdgeOverflow" : false});
        }
    });
